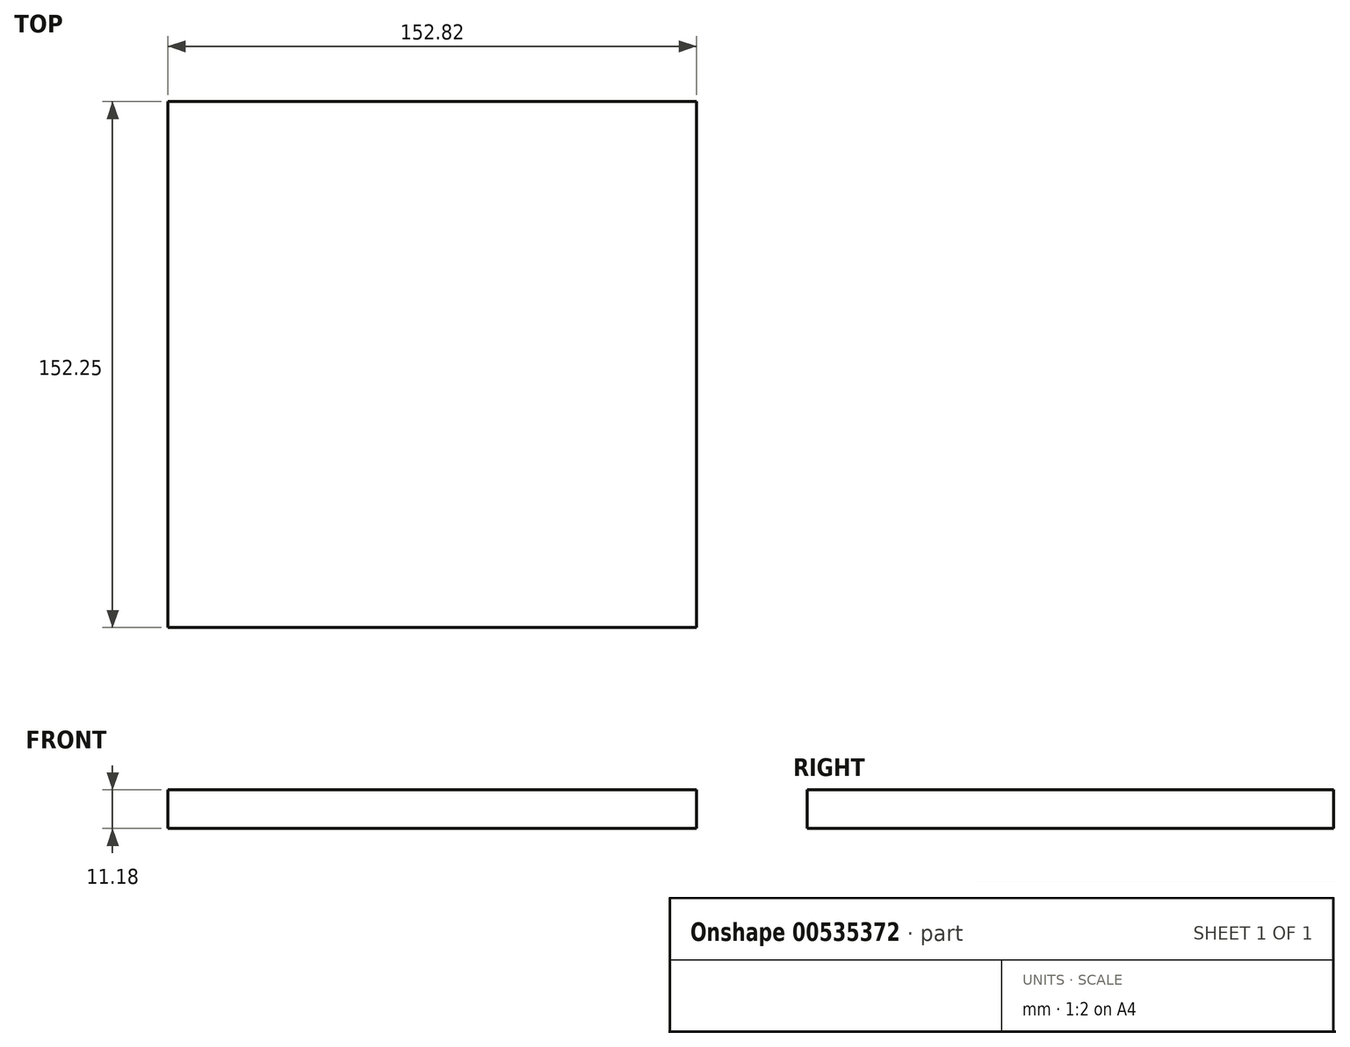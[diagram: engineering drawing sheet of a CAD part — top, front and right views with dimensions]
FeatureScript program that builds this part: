
annotation { "Feature Type Name" : "Feature", "Feature Type Description" : "" }
export const myFeature = defineFeature(function(context is Context, id is Id, definition is map)
    precondition{}
    {
        {
            var Q0;
            Q0=qCreatedBy(makeId("Top.planeOp"),FACE);
            var sketch = newSketch(context, id + "F0", { "sketchPlane" : qUnion([Q0])});
            skLineSegment(sketch, "E0.bottom", {"start": v(-75.98, 75.98) * mm, "end": v(76.84, 75.98) * mm});
            skLineSegment(sketch, "E0.top", {"start": v(-75.98, -76.27) * mm, "end": v(76.84, -76.27) * mm});
            skLineSegment(sketch, "E0.left", {"start": v(-75.98, 75.98) * mm, "end": v(-75.98, -76.27) * mm});
            skLineSegment(sketch, "E0.right", {"start": v(76.84, 75.98) * mm, "end": v(76.84, -76.27) * mm});
            skSolve(sketch);
        }
        {
            var Q0;
            Q0=makeQuery(id+"F0.imprint","IMPRINT",FACE,{"disambiguationData":[TD([[makeQuery(id+"F0.imprint","IMPRINT",EDGE,{"derivedFrom":sQuery(id+"F0.wireOp",EDGE,"E0.bottom")}),-1.0]])]});
            extrude(context, id + "F1", {"entities" : qUnion([Q0]), "depth" : 11.18 * mm, "offsetDistance" : 25.4 * mm});
        }
    });
